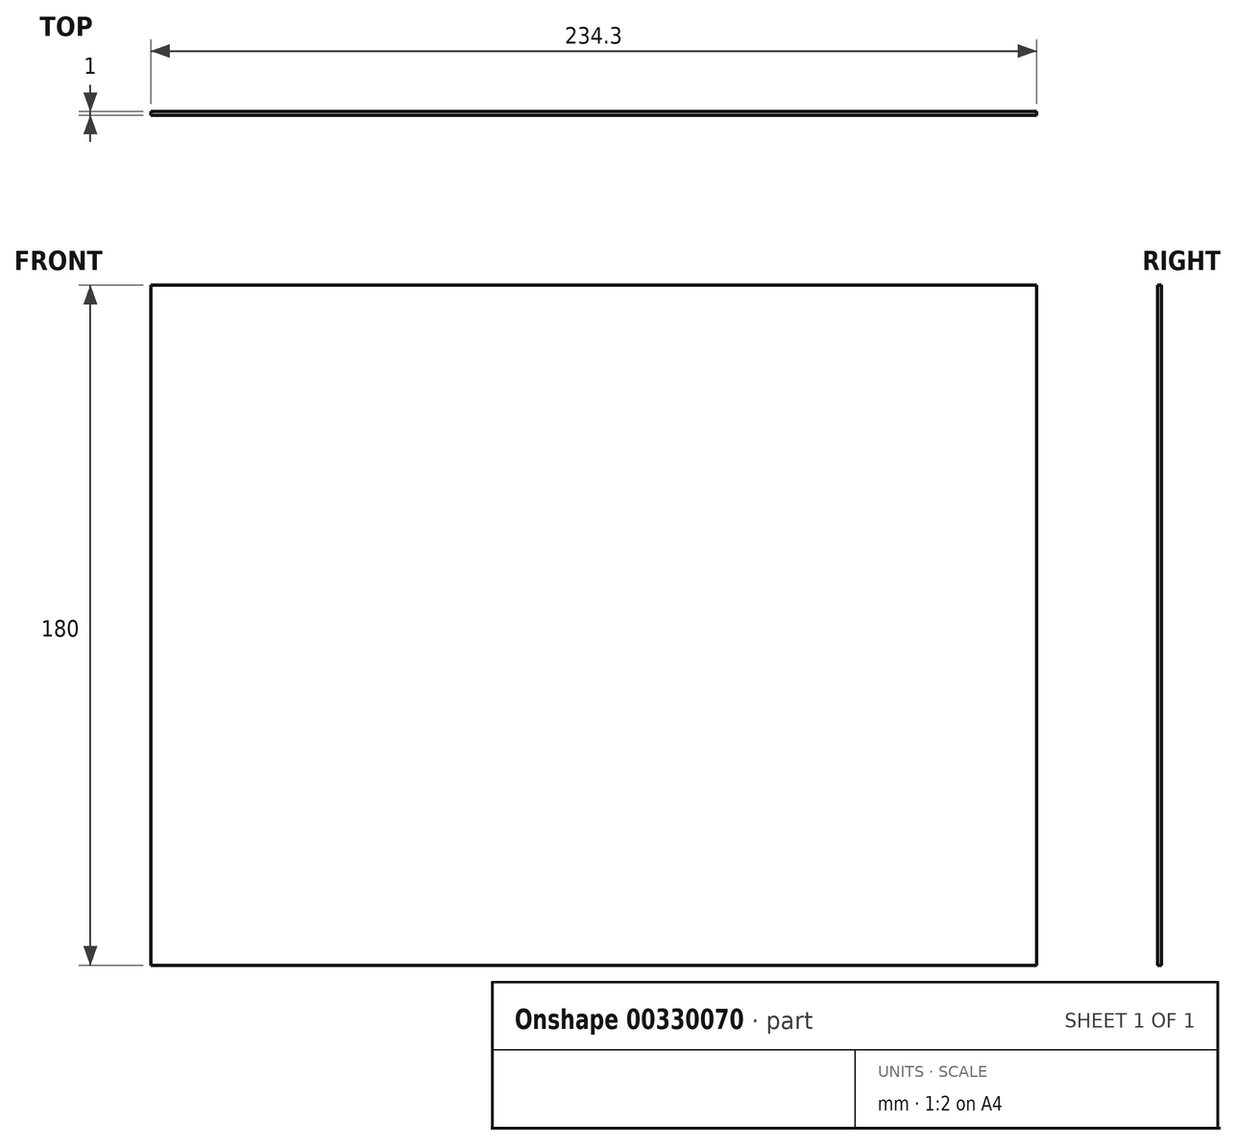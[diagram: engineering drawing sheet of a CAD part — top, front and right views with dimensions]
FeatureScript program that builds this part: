
annotation { "Feature Type Name" : "Feature", "Feature Type Description" : "" }
export const myFeature = defineFeature(function(context is Context, id is Id, definition is map)
    precondition{}
    {
        {
            var Q0;
            Q0=qCreatedBy(makeId("Front.planeOp"),FACE);
            var sketch = newSketch(context, id + "F0", { "sketchPlane" : qUnion([Q0])});
            skLineSegment(sketch, "E0.bottom", {"start": v(-62.68, 190.35) * mm, "end": v(171.62, 190.35) * mm});
            skLineSegment(sketch, "E0.top", {"start": v(-62.68, 10.35) * mm, "end": v(171.62, 10.35) * mm});
            skLineSegment(sketch, "E0.left", {"start": v(-62.68, 190.35) * mm, "end": v(-62.68, 10.35) * mm});
            skLineSegment(sketch, "E0.right", {"start": v(171.62, 190.35) * mm, "end": v(171.62, 10.35) * mm});
            skSolve(sketch);
        }
        {
            var Q0;
            Q0 = qSketchRegion(id + "F0", true);
            extrude(context, id + "F1", {"entities" : qUnion([Q0]), "depth" : 1 * mm, "offsetDistance" : 25 * mm});
        }
    });
